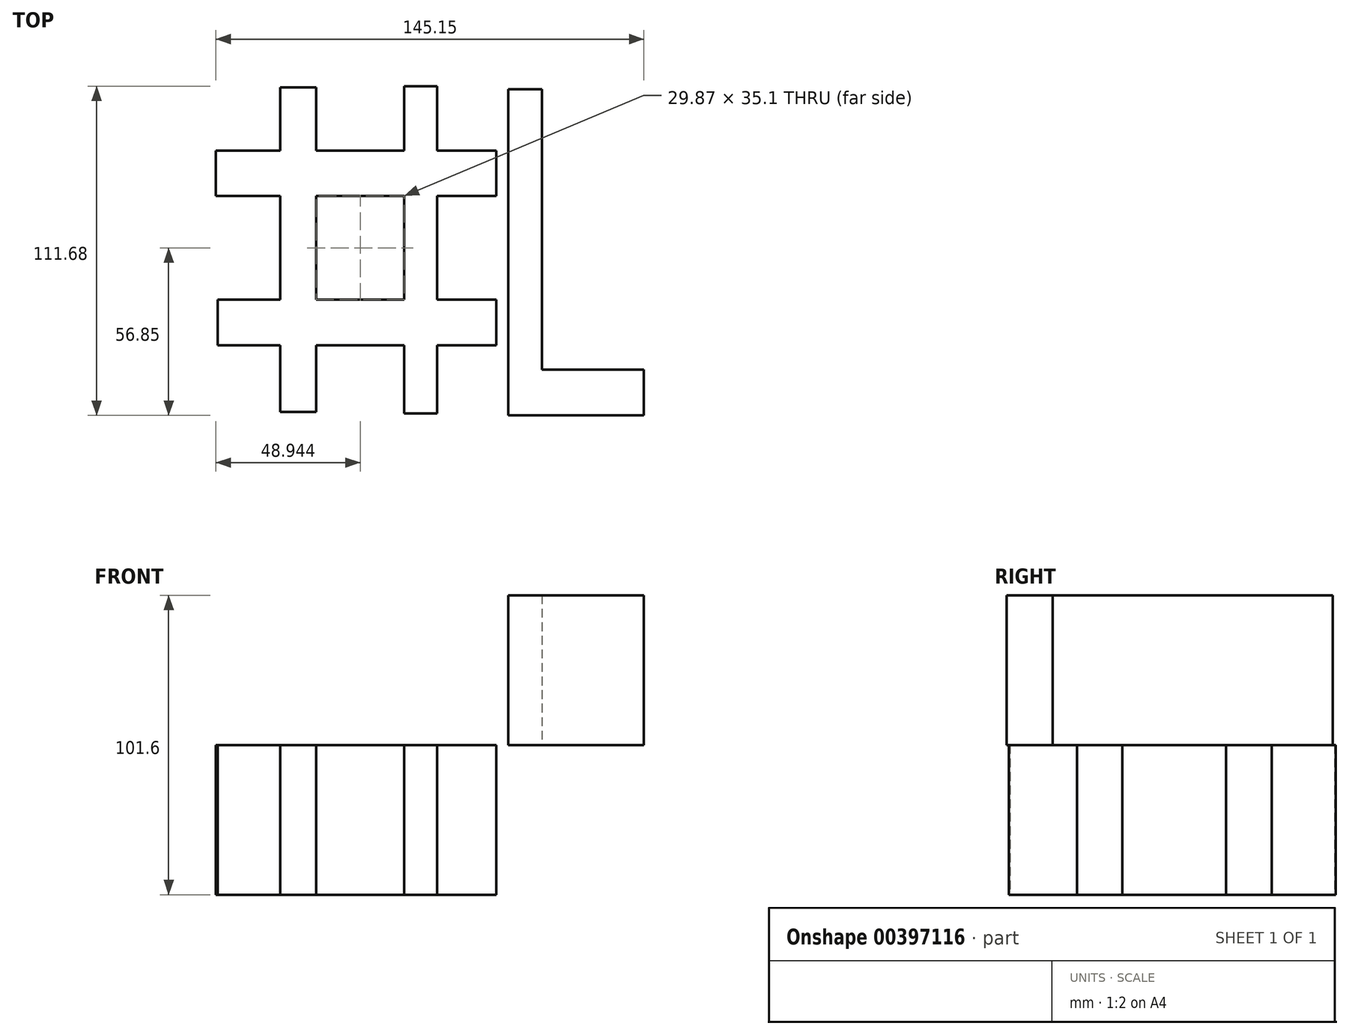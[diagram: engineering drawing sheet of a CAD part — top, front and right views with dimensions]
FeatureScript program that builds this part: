
annotation { "Feature Type Name" : "Feature", "Feature Type Description" : "" }
export const myFeature = defineFeature(function(context is Context, id is Id, definition is map)
    precondition{}
    {
        {
            var Q0;
            Q0=qCreatedBy(makeId("Top.planeOp"),FACE);
            var sketch = newSketch(context, id + "F0", { "sketchPlane" : qUnion([Q0])});
            skLineSegment(sketch, "E0.bottom", {"start": v(-46.22, 36.84) * mm, "end": v(-34, 36.84) * mm});
            skLineSegment(sketch, "E0.top", {"start": v(-46.22, -73.25) * mm, "end": v(-34, -73.25) * mm});
            skLineSegment(sketch, "E0.left", {"start": v(-46.22, 36.84) * mm, "end": v(-46.22, -73.25) * mm});
            skLineSegment(sketch, "E0.right", {"start": v(-34, 36.84) * mm, "end": v(-34, -73.25) * mm});
            skLineSegment(sketch, "E1.bottom", {"start": v(6.98, 37.28) * mm, "end": v(-4.14, 37.28) * mm});
            skLineSegment(sketch, "E1.top", {"start": v(6.98, -73.69) * mm, "end": v(-4.14, -73.69) * mm});
            skLineSegment(sketch, "E1.left", {"start": v(6.98, 37.28) * mm, "end": v(6.98, -73.69) * mm});
            skLineSegment(sketch, "E1.right", {"start": v(-4.14, 37.28) * mm, "end": v(-4.14, -73.69) * mm});
            skLineSegment(sketch, "E2.bottom", {"start": v(-68.02, 15.48) * mm, "end": v(27.03, 15.48) * mm});
            skLineSegment(sketch, "E2.top", {"start": v(-68.02, 0) * mm, "end": v(27.03, 0) * mm});
            skLineSegment(sketch, "E2.left", {"start": v(-68.02, 15.48) * mm, "end": v(-68.02, 0) * mm});
            skLineSegment(sketch, "E2.right", {"start": v(27.03, 15.48) * mm, "end": v(27.03, 0) * mm});
            skLineSegment(sketch, "E3.bottom", {"start": v(-67.37, -35.1) * mm, "end": v(27.03, -35.1) * mm});
            skLineSegment(sketch, "E3.top", {"start": v(-67.37, -50.58) * mm, "end": v(27.03, -50.58) * mm});
            skLineSegment(sketch, "E3.left", {"start": v(-67.37, -35.1) * mm, "end": v(-67.37, -50.58) * mm});
            skLineSegment(sketch, "E3.right", {"start": v(27.03, -35.1) * mm, "end": v(27.03, -50.58) * mm});
            skSolve(sketch);
        }
        {
            var Q0;
            Q0 = qSketchRegion(id + "F0", true);
            extrude(context, id + "F1", {"entities" : qUnion([Q0]), "depth" : 50.8 * mm});
        }
        {
            var Q0;
            Q0=makeQuery(id+"F1.opExtrude","CAP_FACE",FACE,{"disambiguationData":[OSD([sQuery(id+"F0.wireOp",EDGE,"E0.bottom"),sQuery(id+"F0.wireOp",EDGE,"E0.top"),sQuery(id+"F0.wireOp",EDGE,"E0.left"),sQuery(id+"F0.wireOp",EDGE,"E0.right"),sQuery(id+"F0.wireOp",EDGE,"E1.bottom"),sQuery(id+"F0.wireOp",EDGE,"E1.top"),sQuery(id+"F0.wireOp",EDGE,"E1.left"),sQuery(id+"F0.wireOp",EDGE,"E1.right"),sQuery(id+"F0.wireOp",EDGE,"E2.bottom"),sQuery(id+"F0.wireOp",EDGE,"E2.top"),sQuery(id+"F0.wireOp",EDGE,"E2.left"),sQuery(id+"F0.wireOp",EDGE,"E2.right"),sQuery(id+"F0.wireOp",EDGE,"E3.bottom"),sQuery(id+"F0.wireOp",EDGE,"E3.top"),sQuery(id+"F0.wireOp",EDGE,"E3.left"),sQuery(id+"F0.wireOp",EDGE,"E3.right")])],"isStart":false});
            var sketch = newSketch(context, id + "F2", { "sketchPlane" : qUnion([Q0])});
            skLineSegment(sketch, "E4.bottom", {"start": v(31.1, 36.24) * mm, "end": v(42.53, 36.24) * mm});
            skLineSegment(sketch, "E4.top", {"start": v(31.1, -74.4) * mm, "end": v(42.53, -74.4) * mm});
            skLineSegment(sketch, "E4.left", {"start": v(31.1, 36.24) * mm, "end": v(31.1, -74.4) * mm});
            skLineSegment(sketch, "E4.right", {"start": v(42.53, 36.24) * mm, "end": v(42.53, -74.4) * mm});
            skLineSegment(sketch, "E5.bottom", {"start": v(42.53, -58.84) * mm, "end": v(77.13, -58.84) * mm});
            skLineSegment(sketch, "E5.top", {"start": v(42.53, -74.4) * mm, "end": v(77.13, -74.4) * mm});
            skLineSegment(sketch, "E5.left", {"start": v(42.53, -58.84) * mm, "end": v(42.53, -74.4) * mm});
            skLineSegment(sketch, "E5.right", {"start": v(77.13, -58.84) * mm, "end": v(77.13, -74.4) * mm});
            skSolve(sketch);
        }
        {
            var Q0;
            Q0 = qSketchRegion(id + "F2", true);
            extrude(context, id + "F3", {"entities" : qUnion([Q0]), "depth" : 50.8 * mm});
        }
    });
